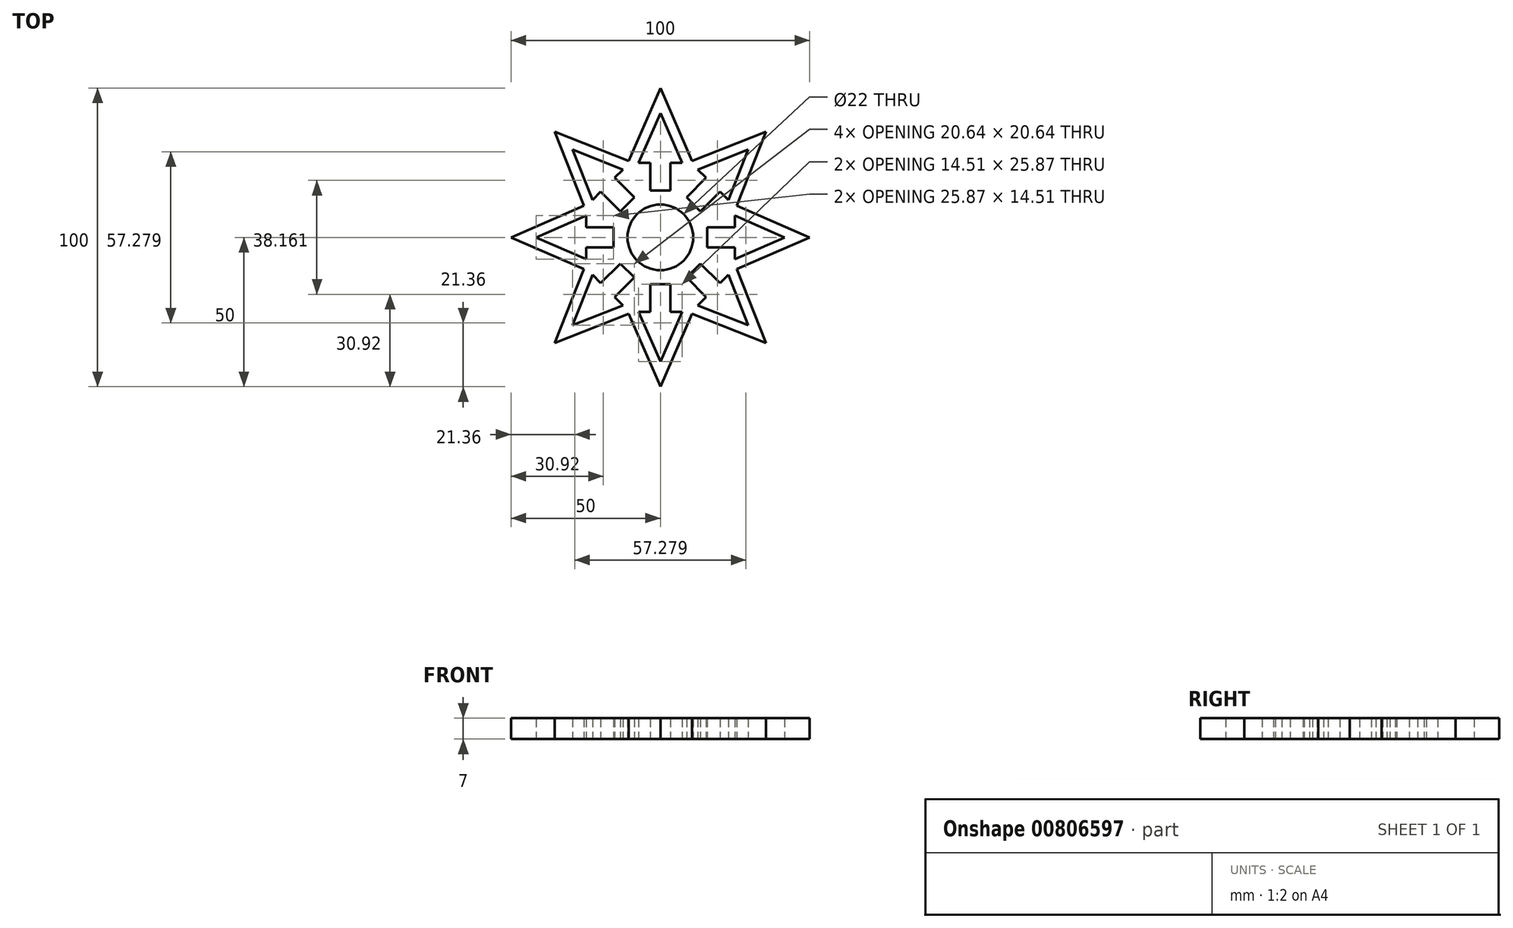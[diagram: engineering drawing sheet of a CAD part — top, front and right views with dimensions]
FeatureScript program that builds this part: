
annotation { "Feature Type Name" : "Feature", "Feature Type Description" : "" }
export const myFeature = defineFeature(function(context is Context, id is Id, definition is map)
    precondition{}
    {
        {
            var Q0;
            Q0=qCreatedBy(makeId("Top.planeOp"),FACE);
            var sketch = newSketch(context, id + "F0", { "sketchPlane" : qUnion([Q0])});
            skCircle(sketch, "E0", {"center": v(0, 0) * mm, "radius": 11 * mm});
            skLineSegment(sketch, "E1", {"start": v(-10.6, 25.6) * mm, "end": v(0, 50) * mm});
            skLineSegment(sketch, "E2.MirrorCS", {"start": v(10.6, 25.6) * mm, "end": v(0, 50) * mm});
            skLineSegment(sketch, "E3.1.0", {"start": v(-25.6, 10.6) * mm, "end": v(-35.36, 35.36) * mm});
            skLineSegment(sketch, "E3.1.1", {"start": v(-10.6, 25.6) * mm, "end": v(-35.36, 35.36) * mm});
            skLineSegment(sketch, "E3.2.0", {"start": v(-25.6, -10.6) * mm, "end": v(-50, 0) * mm});
            skLineSegment(sketch, "E3.2.1", {"start": v(-25.6, 10.6) * mm, "end": v(-50, 0) * mm});
            skLineSegment(sketch, "E3.3.0", {"start": v(-10.6, -25.6) * mm, "end": v(-35.36, -35.36) * mm});
            skLineSegment(sketch, "E3.3.1", {"start": v(-25.6, -10.6) * mm, "end": v(-35.36, -35.36) * mm});
            skLineSegment(sketch, "E3.4.0", {"start": v(10.6, -25.6) * mm, "end": v(0, -50) * mm});
            skLineSegment(sketch, "E3.4.1", {"start": v(-10.6, -25.6) * mm, "end": v(0, -50) * mm});
            skLineSegment(sketch, "E3.5.0", {"start": v(25.6, -10.6) * mm, "end": v(35.36, -35.36) * mm});
            skLineSegment(sketch, "E3.5.1", {"start": v(10.6, -25.6) * mm, "end": v(35.36, -35.36) * mm});
            skLineSegment(sketch, "E3.6.0", {"start": v(25.6, 10.6) * mm, "end": v(50, 0) * mm});
            skLineSegment(sketch, "E3.6.1", {"start": v(25.6, -10.6) * mm, "end": v(50, 0) * mm});
            skLineSegment(sketch, "E3.7.0", {"start": v(10.6, 25.6) * mm, "end": v(35.36, 35.36) * mm});
            skLineSegment(sketch, "E3.7.1", {"start": v(25.6, 10.6) * mm, "end": v(35.36, 35.36) * mm});
            skPoint(sketch, "E4.orphan", {"position": v(-21.21, 21.21) * mm});
            skPoint(sketch, "E5.7.end.orphan", {"position": v(0, 30) * mm});
            skLineSegment(sketch, "E6", {"start": v(0, 41.58) * mm, "end": v(-7.25, 24.9) * mm});
            skLineSegment(sketch, "E7", {"start": v(-7.25, 24.9) * mm, "end": v(-3.31, 24.9) * mm});
            skLineSegment(sketch, "E8", {"start": v(-3.31, 24.9) * mm, "end": v(-3.31, 15.7) * mm});
            skLineSegment(sketch, "E9", {"start": v(-3.31, 15.7) * mm, "end": v(0, 15.7) * mm});
            skLineSegment(sketch, "E10.MirrorCS", {"start": v(0, 41.58) * mm, "end": v(7.25, 24.9) * mm});
            skLineSegment(sketch, "E11.MirrorCS", {"start": v(7.25, 24.9) * mm, "end": v(3.31, 24.9) * mm});
            skLineSegment(sketch, "E12.MirrorCS", {"start": v(3.31, 24.9) * mm, "end": v(3.31, 15.7) * mm});
            skLineSegment(sketch, "E13.MirrorCS", {"start": v(3.31, 15.7) * mm, "end": v(0, 15.7) * mm});
            skLineSegment(sketch, "E14.1.0", {"start": v(-29.4, 29.4) * mm, "end": v(-12.48, 22.73) * mm});
            skLineSegment(sketch, "E14.1.1", {"start": v(-29.4, 29.4) * mm, "end": v(-22.73, 12.48) * mm});
            skLineSegment(sketch, "E14.1.2", {"start": v(-22.73, 12.48) * mm, "end": v(-19.95, 15.26) * mm});
            skLineSegment(sketch, "E14.1.3", {"start": v(-19.95, 15.26) * mm, "end": v(-13.44, 8.76) * mm});
            skLineSegment(sketch, "E14.1.4", {"start": v(-13.44, 8.76) * mm, "end": v(-11.1, 11.1) * mm});
            skLineSegment(sketch, "E14.1.5", {"start": v(-8.76, 13.44) * mm, "end": v(-11.1, 11.1) * mm});
            skLineSegment(sketch, "E14.1.6", {"start": v(-15.26, 19.95) * mm, "end": v(-8.76, 13.44) * mm});
            skLineSegment(sketch, "E14.1.7", {"start": v(-12.48, 22.73) * mm, "end": v(-15.26, 19.95) * mm});
            skLineSegment(sketch, "E14.2.0", {"start": v(-41.58, 0) * mm, "end": v(-24.9, 7.25) * mm});
            skLineSegment(sketch, "E14.2.1", {"start": v(-41.58, 0) * mm, "end": v(-24.9, -7.25) * mm});
            skLineSegment(sketch, "E14.2.2", {"start": v(-24.9, -7.25) * mm, "end": v(-24.9, -3.31) * mm});
            skLineSegment(sketch, "E14.2.3", {"start": v(-24.9, -3.31) * mm, "end": v(-15.7, -3.31) * mm});
            skLineSegment(sketch, "E14.2.4", {"start": v(-15.7, -3.31) * mm, "end": v(-15.7, 0) * mm});
            skLineSegment(sketch, "E14.2.5", {"start": v(-15.7, 3.31) * mm, "end": v(-15.7, 0) * mm});
            skLineSegment(sketch, "E14.2.6", {"start": v(-24.9, 3.31) * mm, "end": v(-15.7, 3.31) * mm});
            skLineSegment(sketch, "E14.2.7", {"start": v(-24.9, 7.25) * mm, "end": v(-24.9, 3.31) * mm});
            skLineSegment(sketch, "E14.3.0", {"start": v(-29.4, -29.4) * mm, "end": v(-22.73, -12.48) * mm});
            skLineSegment(sketch, "E14.3.1", {"start": v(-29.4, -29.4) * mm, "end": v(-12.48, -22.73) * mm});
            skLineSegment(sketch, "E14.3.2", {"start": v(-12.48, -22.73) * mm, "end": v(-15.26, -19.95) * mm});
            skLineSegment(sketch, "E14.3.3", {"start": v(-15.26, -19.95) * mm, "end": v(-8.76, -13.44) * mm});
            skLineSegment(sketch, "E14.3.4", {"start": v(-8.76, -13.44) * mm, "end": v(-11.1, -11.1) * mm});
            skLineSegment(sketch, "E14.3.5", {"start": v(-13.44, -8.76) * mm, "end": v(-11.1, -11.1) * mm});
            skLineSegment(sketch, "E14.3.6", {"start": v(-19.95, -15.26) * mm, "end": v(-13.44, -8.76) * mm});
            skLineSegment(sketch, "E14.3.7", {"start": v(-22.73, -12.48) * mm, "end": v(-19.95, -15.26) * mm});
            skLineSegment(sketch, "E14.4.0", {"start": v(0, -41.58) * mm, "end": v(-7.25, -24.9) * mm});
            skLineSegment(sketch, "E14.4.1", {"start": v(0, -41.58) * mm, "end": v(7.25, -24.9) * mm});
            skLineSegment(sketch, "E14.4.2", {"start": v(7.25, -24.9) * mm, "end": v(3.31, -24.9) * mm});
            skLineSegment(sketch, "E14.4.3", {"start": v(3.31, -24.9) * mm, "end": v(3.31, -15.7) * mm});
            skLineSegment(sketch, "E14.4.4", {"start": v(3.31, -15.7) * mm, "end": v(0, -15.7) * mm});
            skLineSegment(sketch, "E14.4.5", {"start": v(-3.31, -15.7) * mm, "end": v(0, -15.7) * mm});
            skLineSegment(sketch, "E14.4.6", {"start": v(-3.31, -24.9) * mm, "end": v(-3.31, -15.7) * mm});
            skLineSegment(sketch, "E14.4.7", {"start": v(-7.25, -24.9) * mm, "end": v(-3.31, -24.9) * mm});
            skLineSegment(sketch, "E14.5.0", {"start": v(29.4, -29.4) * mm, "end": v(12.48, -22.73) * mm});
            skLineSegment(sketch, "E14.5.1", {"start": v(29.4, -29.4) * mm, "end": v(22.73, -12.48) * mm});
            skLineSegment(sketch, "E14.5.2", {"start": v(22.73, -12.48) * mm, "end": v(19.95, -15.26) * mm});
            skLineSegment(sketch, "E14.5.3", {"start": v(19.95, -15.26) * mm, "end": v(13.44, -8.76) * mm});
            skLineSegment(sketch, "E14.5.4", {"start": v(13.44, -8.76) * mm, "end": v(11.1, -11.1) * mm});
            skLineSegment(sketch, "E14.5.5", {"start": v(8.76, -13.44) * mm, "end": v(11.1, -11.1) * mm});
            skLineSegment(sketch, "E14.5.6", {"start": v(15.26, -19.95) * mm, "end": v(8.76, -13.44) * mm});
            skLineSegment(sketch, "E14.5.7", {"start": v(12.48, -22.73) * mm, "end": v(15.26, -19.95) * mm});
            skLineSegment(sketch, "E14.6.0", {"start": v(41.58, 0) * mm, "end": v(24.9, -7.25) * mm});
            skLineSegment(sketch, "E14.6.1", {"start": v(41.58, 0) * mm, "end": v(24.9, 7.25) * mm});
            skLineSegment(sketch, "E14.6.2", {"start": v(24.9, 7.25) * mm, "end": v(24.9, 3.31) * mm});
            skLineSegment(sketch, "E14.6.3", {"start": v(24.9, 3.31) * mm, "end": v(15.7, 3.31) * mm});
            skLineSegment(sketch, "E14.6.4", {"start": v(15.7, 3.31) * mm, "end": v(15.7, 0) * mm});
            skLineSegment(sketch, "E14.6.5", {"start": v(15.7, -3.31) * mm, "end": v(15.7, 0) * mm});
            skLineSegment(sketch, "E14.6.6", {"start": v(24.9, -3.31) * mm, "end": v(15.7, -3.31) * mm});
            skLineSegment(sketch, "E14.6.7", {"start": v(24.9, -7.25) * mm, "end": v(24.9, -3.31) * mm});
            skLineSegment(sketch, "E14.7.0", {"start": v(29.4, 29.4) * mm, "end": v(22.73, 12.48) * mm});
            skLineSegment(sketch, "E14.7.1", {"start": v(29.4, 29.4) * mm, "end": v(12.48, 22.73) * mm});
            skLineSegment(sketch, "E14.7.2", {"start": v(12.48, 22.73) * mm, "end": v(15.26, 19.95) * mm});
            skLineSegment(sketch, "E14.7.3", {"start": v(15.26, 19.95) * mm, "end": v(8.76, 13.44) * mm});
            skLineSegment(sketch, "E14.7.4", {"start": v(8.76, 13.44) * mm, "end": v(11.1, 11.1) * mm});
            skLineSegment(sketch, "E14.7.5", {"start": v(13.44, 8.76) * mm, "end": v(11.1, 11.1) * mm});
            skLineSegment(sketch, "E14.7.6", {"start": v(19.95, 15.26) * mm, "end": v(13.44, 8.76) * mm});
            skLineSegment(sketch, "E14.7.7", {"start": v(22.73, 12.48) * mm, "end": v(19.95, 15.26) * mm});
            skSolve(sketch);
        }
        {
            var Q0;
            Q0 = qSketchRegion(id + "F0", true);
            extrude(context, id + "F1", {"entities" : qUnion([Q0]), "depth" : 7 * mm, "offsetDistance" : 25 * mm});
        }
    });
